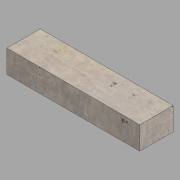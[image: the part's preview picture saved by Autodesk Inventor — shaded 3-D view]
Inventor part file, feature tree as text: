
AUTODESK INVENTOR PART (.ipt)
format: ipt  version: 2022 (Build 260153000, 153)  size: 116,224 bytes
history: native  units: in
note: dims shown in document units (in); Inventor stores cm internally (conversion verified against a paired STEP export)
features: other x1, extrude x1, sketch x1
ambient origin geometry x8: Origin, YZ Plane, XZ Plane, XY Plane, X Axis, Y Axis, Z Axis, Center Point
bodies: Body1 (feature_tree)
feature tree (3):
  other  "Type 2 paver vehicular"
  extrude  "Extrusion1"  Depth=6.0in
  sketch  "Sketch1"  dims[d0=23.9062in d1=6.0in d2=4.125in d3=0.0in]
